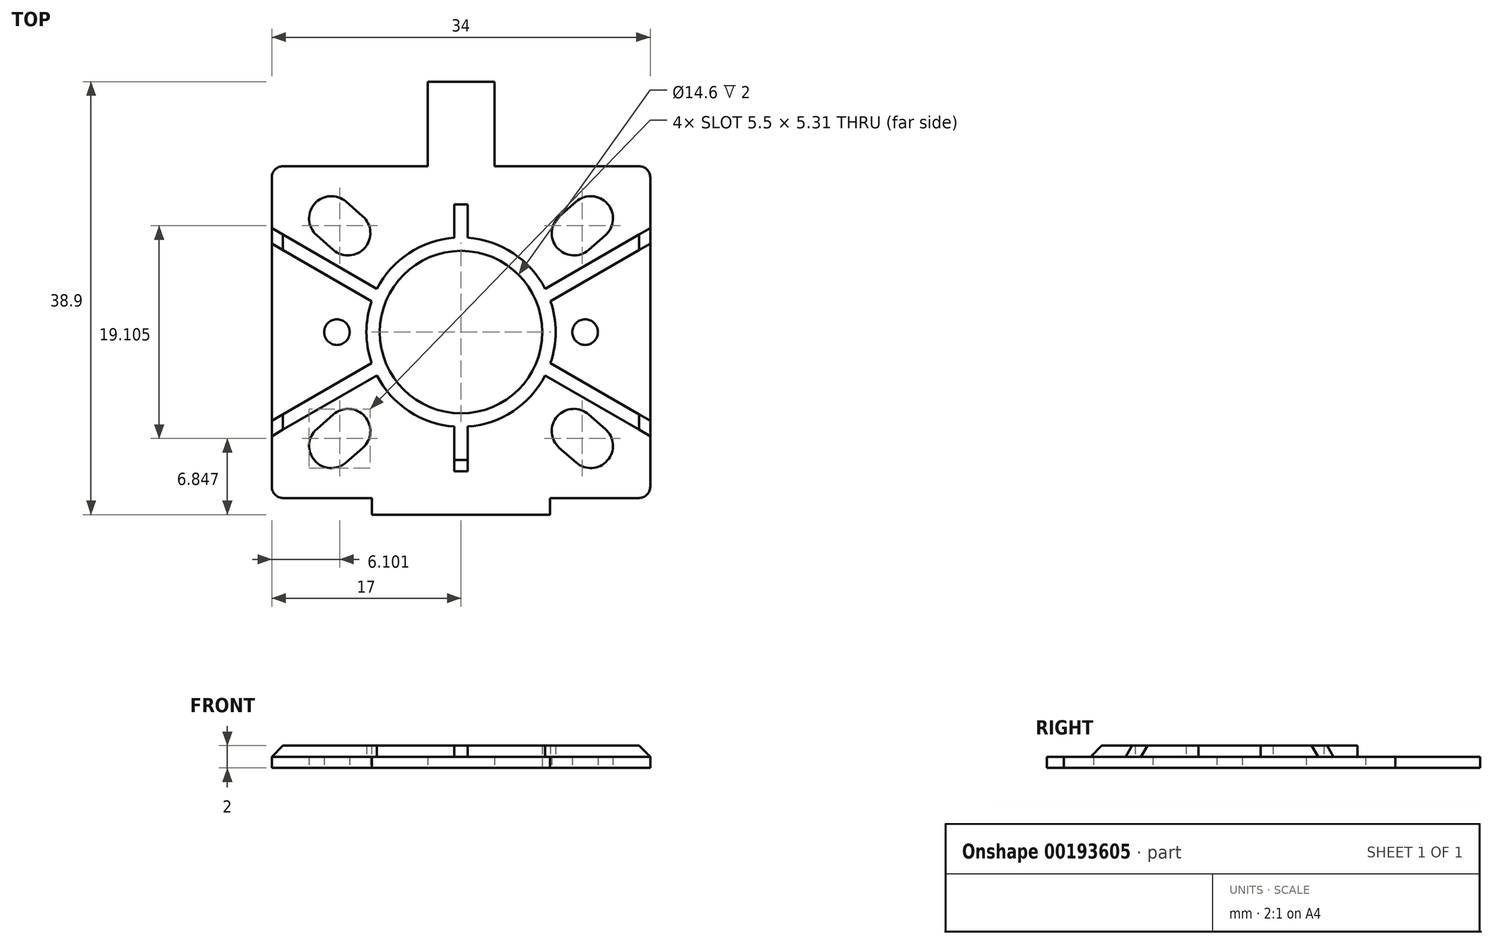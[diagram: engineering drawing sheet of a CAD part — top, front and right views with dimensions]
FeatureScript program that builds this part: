
annotation { "Feature Type Name" : "Feature", "Feature Type Description" : "" }
export const myFeature = defineFeature(function(context is Context, id is Id, definition is map)
    precondition{}
    {
        {
            var Q0;
            Q0=qCreatedBy(makeId("Top.planeOp"),FACE);
            var sketch = newSketch(context, id + "F0", { "sketchPlane" : qUnion([Q0])});
            skLineSegment(sketch, "E0.bottom", {"start": v(16, -14.9) * mm, "end": v(-16, -14.9) * mm});
            skLineSegment(sketch, "E0.top", {"start": v(16, 14.9) * mm, "end": v(-16, 14.9) * mm});
            skLineSegment(sketch, "E0.left", {"start": v(17, -13.9) * mm, "end": v(17, 13.9) * mm});
            skLineSegment(sketch, "E0.right", {"start": v(-17, -13.9) * mm, "end": v(-17, 13.9) * mm});
            skPoint(sketch, "E0.middle", {"position": v(0, 0) * mm});
            skCircle(sketch, "E1", {"center": v(0, 0) * mm, "radius": 7.3 * mm});
            skLineSegment(sketch, "E2", {"start": v(-11.15, 0) * mm, "end": v(11.15, 0) * mm, "construction": true});
            skCircle(sketch, "E3", {"center": v(-11.15, 0) * mm, "radius": 1.15 * mm});
            skCircle(sketch, "E4", {"center": v(11.15, 0) * mm, "radius": 1.15 * mm});
            skLineSegment(sketch, "E5.bottom", {"start": v(3, 14.9) * mm, "end": v(-3, 14.9) * mm});
            skLineSegment(sketch, "E5.top", {"start": v(3, 22.5) * mm, "end": v(-3, 22.5) * mm});
            skLineSegment(sketch, "E5.left", {"start": v(3, 14.9) * mm, "end": v(3, 22.5) * mm});
            skLineSegment(sketch, "E5.right", {"start": v(-3, 14.9) * mm, "end": v(-3, 22.5) * mm});
            skPoint(sketch, "E5.middle", {"position": v(0, 18.7) * mm});
            skLineSegment(sketch, "E6.bottom", {"start": v(8, -16.4) * mm, "end": v(-8, -16.4) * mm});
            skLineSegment(sketch, "E6.top", {"start": v(8, -14.9) * mm, "end": v(-8, -14.9) * mm});
            skLineSegment(sketch, "E6.left", {"start": v(8, -16.4) * mm, "end": v(8, -14.9) * mm});
            skLineSegment(sketch, "E6.right", {"start": v(-8, -16.4) * mm, "end": v(-8, -14.9) * mm});
            skPoint(sketch, "E6.middle", {"position": v(0, -15.65) * mm});
            skPoint(sketch, "E6.middle.positionSnap0", {"position": v(0, -14.9) * mm});
            skPoint(sketch, "E6.centerSnap0", {"position": v(0, -14.9) * mm});
            skLineSegment(sketch, "E7", {"start": v(-17, 14.9) * mm, "end": v(17, -14.9) * mm, "construction": true});
            skLineSegment(sketch, "E8", {"start": v(-17, -14.9) * mm, "end": v(17, 14.9) * mm, "construction": true});
            skLineSegment(sketch, "E9", {"start": v(0, -14.9) * mm, "end": v(0, 14.9) * mm, "construction": true});
            skPoint(sketch, "E10.visualSharp", {"position": v(-17, 14.9) * mm});
            skArc(sketch, "E10.filletArc", {"start": v(-16, 14.9) * mm, "mid": v(-16.7, 14.6) * mm, "end": v(-17, 13.9) * mm});
            skPoint(sketch, "E11.visualSharp", {"position": v(17, 14.9) * mm});
            skArc(sketch, "E11.filletArc", {"start": v(17, 13.9) * mm, "mid": v(16.7, 14.6) * mm, "end": v(16, 14.9) * mm});
            skPoint(sketch, "E12.visualSharp", {"position": v(17, -14.9) * mm});
            skArc(sketch, "E12.filletArc", {"start": v(16, -14.9) * mm, "mid": v(16.7, -14.6) * mm, "end": v(17, -13.9) * mm});
            skPoint(sketch, "E13.visualSharp", {"position": v(-17, -14.9) * mm});
            skArc(sketch, "E13.filletArc", {"start": v(-17, -13.9) * mm, "mid": v(-16.7, -14.6) * mm, "end": v(-16, -14.9) * mm});
            skLineSegment(sketch, "E14", {"start": v(-11.65, 10.21) * mm, "end": v(-10.15, 8.9) * mm, "construction": true});
            skArc(sketch, "E15.0.startCap", {"start": v(-12.97, 8.7) * mm, "mid": v(-13.15, 11.53) * mm, "end": v(-10.33, 11.72) * mm});
            skArc(sketch, "E15.0.endCap", {"start": v(-8.83, 10.4) * mm, "mid": v(-8.64, 7.58) * mm, "end": v(-11.47, 7.39) * mm});
            skLineSegment(sketch, "E15.0.left", {"start": v(-10.33, 11.72) * mm, "end": v(-8.83, 10.4) * mm});
            skLineSegment(sketch, "E15.0.right", {"start": v(-12.97, 8.7) * mm, "end": v(-11.47, 7.39) * mm});
            skLineSegment(sketch, "E16.MirrorCS", {"start": v(11.65, 10.21) * mm, "end": v(10.15, 8.9) * mm, "construction": true});
            skLineSegment(sketch, "E17.MirrorCS", {"start": v(12.97, 8.7) * mm, "end": v(11.47, 7.39) * mm});
            skArc(sketch, "E18.MirrorCS", {"start": v(8.83, 10.4) * mm, "mid": v(8.64, 7.58) * mm, "end": v(11.47, 7.39) * mm});
            skLineSegment(sketch, "E19.MirrorCS", {"start": v(10.33, 11.72) * mm, "end": v(8.83, 10.4) * mm});
            skArc(sketch, "E20.MirrorCS", {"start": v(12.97, 8.7) * mm, "mid": v(13.15, 11.53) * mm, "end": v(10.33, 11.72) * mm});
            skLineSegment(sketch, "E21.MirrorCS", {"start": v(10.33, -11.72) * mm, "end": v(8.83, -10.4) * mm});
            skLineSegment(sketch, "E22.MirrorCS", {"start": v(-10.33, -11.72) * mm, "end": v(-8.83, -10.4) * mm});
            skLineSegment(sketch, "E23.MirrorCS", {"start": v(-11.65, -10.21) * mm, "end": v(-10.15, -8.9) * mm, "construction": true});
            skLineSegment(sketch, "E24.MirrorCS", {"start": v(11.65, -10.21) * mm, "end": v(10.15, -8.9) * mm, "construction": true});
            skLineSegment(sketch, "E25.MirrorCS", {"start": v(-12.97, -8.7) * mm, "end": v(-11.47, -7.39) * mm});
            skLineSegment(sketch, "E26.MirrorCS", {"start": v(12.97, -8.7) * mm, "end": v(11.47, -7.39) * mm});
            skArc(sketch, "E27.MirrorCS", {"start": v(-8.83, -10.4) * mm, "mid": v(-8.64, -7.58) * mm, "end": v(-11.47, -7.39) * mm});
            skArc(sketch, "E28.MirrorCS", {"start": v(12.97, -8.7) * mm, "mid": v(13.15, -11.53) * mm, "end": v(10.33, -11.72) * mm});
            skArc(sketch, "E29.MirrorCS", {"start": v(-12.97, -8.7) * mm, "mid": v(-13.15, -11.53) * mm, "end": v(-10.33, -11.72) * mm});
            skArc(sketch, "E30.MirrorCS", {"start": v(8.83, -10.4) * mm, "mid": v(8.64, -7.58) * mm, "end": v(11.47, -7.39) * mm});
            skSolve(sketch);
        }
        {
            var Q0;
            Q0 = qSketchRegion(id + "F0", true);
            extrude(context, id + "F1", {"entities" : qUnion([Q0]), "depth" : 1 * mm});
        }
        {
            var Q0;
            Q0=makeQuery(id+"F1.opExtrude","CAP_FACE",FACE,{"disambiguationData":[OSD([sQuery(id+"F0.wireOp",EDGE,"E0.bottom"),sQuery(id+"F0.wireOp",EDGE,"E0.top"),sQuery(id+"F0.wireOp",EDGE,"E0.left"),sQuery(id+"F0.wireOp",EDGE,"E0.right"),sQuery(id+"F0.wireOp",EDGE,"E1"),sQuery(id+"F0.wireOp",EDGE,"E3"),sQuery(id+"F0.wireOp",EDGE,"E4"),sQuery(id+"F0.wireOp",EDGE,"E5.top"),sQuery(id+"F0.wireOp",EDGE,"E5.left"),sQuery(id+"F0.wireOp",EDGE,"E5.right"),sQuery(id+"F0.wireOp",EDGE,"E6.bottom"),sQuery(id+"F0.wireOp",EDGE,"E6.left"),sQuery(id+"F0.wireOp",EDGE,"E6.right"),sQuery(id+"F0.wireOp",EDGE,"Cg5mHujw-Crgq-w9C2-tdzf-h039JNJG8W8y"),sQuery(id+"F0.wireOp",EDGE,"Ps9XZvL5-BTdY-0Dsp-DGuL-4wo60B738f9t"),sQuery(id+"F0.wireOp",EDGE,"NziZYGv3-ZalC-V9XH-VD5N-91aEUs1mGeD4"),sQuery(id+"F0.wireOp",EDGE,"wrparZR5-Ca0K-EmIK-8Wlq-3zDmcIoanExd"),sQuery(id+"F0.wireOp",EDGE,"30673667-c7c9-486b-8852-d69ce27fa3a1.filletArc"),sQuery(id+"F0.wireOp",EDGE,"ba702d56-8ab8-4f31-9c18-c75d7e6bf162.filletArc"),sQuery(id+"F0.wireOp",EDGE,"61057ac9-38be-461f-bca9-094edfcdb327.filletArc"),sQuery(id+"F0.wireOp",EDGE,"a9f16732-ca3d-4a78-8be7-feecf1bcdde3.filletArc"),sQuery(id+"F0.wireOp",EDGE,"0958a51f-cc26-4892-b37d-54eeb7879d5b0.MirrorCS"),sQuery(id+"F0.wireOp",EDGE,"0958a51f-cc26-4892-b37d-54eeb7879d5b1.MirrorCS"),sQuery(id+"F0.wireOp",EDGE,"0958a51f-cc26-4892-b37d-54eeb7879d5b2.MirrorCS"),sQuery(id+"F0.wireOp",EDGE,"0958a51f-cc26-4892-b37d-54eeb7879d5b3.MirrorCS"),sQuery(id+"F0.wireOp",EDGE,"0958a51f-cc26-4892-b37d-54eeb7879d5b4.MirrorCS"),sQuery(id+"F0.wireOp",EDGE,"0958a51f-cc26-4892-b37d-54eeb7879d5b6.MirrorCS"),sQuery(id+"F0.wireOp",EDGE,"0958a51f-cc26-4892-b37d-54eeb7879d5b8.MirrorCS"),sQuery(id+"F0.wireOp",EDGE,"0958a51f-cc26-4892-b37d-54eeb7879d5b11.MirrorCS"),sQuery(id+"F0.wireOp",EDGE,"47bd3fab-0a37-40e4-8793-955853e768a70.MirrorCS"),sQuery(id+"F0.wireOp",EDGE,"47bd3fab-0a37-40e4-8793-955853e768a71.MirrorCS"),sQuery(id+"F0.wireOp",EDGE,"47bd3fab-0a37-40e4-8793-955853e768a72.MirrorCS"),sQuery(id+"F0.wireOp",EDGE,"47bd3fab-0a37-40e4-8793-955853e768a73.MirrorCS"),sQuery(id+"F0.wireOp",EDGE,"47bd3fab-0a37-40e4-8793-955853e768a74.MirrorCS"),sQuery(id+"F0.wireOp",EDGE,"47bd3fab-0a37-40e4-8793-955853e768a75.MirrorCS"),sQuery(id+"F0.wireOp",EDGE,"47bd3fab-0a37-40e4-8793-955853e768a76.MirrorCS"),sQuery(id+"F0.wireOp",EDGE,"47bd3fab-0a37-40e4-8793-955853e768a77.MirrorCS"),sQuery(id+"F0.wireOp",EDGE,"47bd3fab-0a37-40e4-8793-955853e768a78.MirrorCS"),sQuery(id+"F0.wireOp",EDGE,"47bd3fab-0a37-40e4-8793-955853e768a79.MirrorCS"),sQuery(id+"F0.wireOp",EDGE,"47bd3fab-0a37-40e4-8793-955853e768a710.MirrorCS"),sQuery(id+"F0.wireOp",EDGE,"47bd3fab-0a37-40e4-8793-955853e768a711.MirrorCS"),sQuery(id+"F0.wireOp",EDGE,"47bd3fab-0a37-40e4-8793-955853e768a712.MirrorCS"),sQuery(id+"F0.wireOp",EDGE,"47bd3fab-0a37-40e4-8793-955853e768a718.MirrorCS"),sQuery(id+"F0.wireOp",EDGE,"47bd3fab-0a37-40e4-8793-955853e768a722.MirrorCS"),sQuery(id+"F0.wireOp",EDGE,"47bd3fab-0a37-40e4-8793-955853e768a723.MirrorCS"),sQuery(id+"F0.wireOp",EDGE,"E10.filletArc"),sQuery(id+"F0.wireOp",EDGE,"E11.filletArc"),sQuery(id+"F0.wireOp",EDGE,"E12.filletArc"),sQuery(id+"F0.wireOp",EDGE,"E13.filletArc")])],"isStart":false});
            var sketch = newSketch(context, id + "F2", { "sketchPlane" : qUnion([Q0])});
            skCircle(sketch, "E31.0", {"center": v(0, 0) * mm, "radius": 7.3 * mm});
            skCircle(sketch, "E32.0", {"center": v(0, 0) * mm, "radius": 8.5 * mm});
            skLineSegment(sketch, "E33", {"start": v(0, 14.9) * mm, "end": v(0, -14.9) * mm, "construction": true});
            skLineSegment(sketch, "E34", {"start": v(-17, 0) * mm, "end": v(17, 0) * mm, "construction": true});
            skLineSegment(sketch, "E35", {"start": v(-17, 9.34) * mm, "end": v(-7.56, 3.9) * mm});
            skLineSegment(sketch, "E36", {"start": v(-17, 7.96) * mm, "end": v(-8.03, 2.78) * mm});
            skLineSegment(sketch, "E37.MirrorCS", {"start": v(-17, -7.96) * mm, "end": v(-8.03, -2.78) * mm});
            skLineSegment(sketch, "E38.MirrorCS", {"start": v(-17, -9.34) * mm, "end": v(-7.56, -3.9) * mm});
            skLineSegment(sketch, "E39.MirrorCS", {"start": v(17, 9.34) * mm, "end": v(7.56, 3.9) * mm});
            skLineSegment(sketch, "E40.MirrorCS", {"start": v(17, 7.96) * mm, "end": v(8.03, 2.78) * mm});
            skLineSegment(sketch, "E41.MirrorCS", {"start": v(17, -7.96) * mm, "end": v(8.03, -2.78) * mm});
            skLineSegment(sketch, "E42.MirrorCS", {"start": v(17, -9.34) * mm, "end": v(7.56, -3.9) * mm});
            skLineSegment(sketch, "E43.bottom", {"start": v(0.6, 7.3) * mm, "end": v(-0.6, 7.3) * mm});
            skLineSegment(sketch, "E43.top", {"start": v(0.6, 11.48) * mm, "end": v(-0.6, 11.48) * mm});
            skLineSegment(sketch, "E43.left", {"start": v(0.6, 7.3) * mm, "end": v(0.6, 11.48) * mm});
            skLineSegment(sketch, "E43.right", {"start": v(-0.6, 7.3) * mm, "end": v(-0.6, 11.48) * mm});
            skPoint(sketch, "E43.middle", {"position": v(0, 9.4) * mm});
            skLineSegment(sketch, "E44.MirrorCS", {"start": v(0.6, -11.48) * mm, "end": v(-0.6, -11.48) * mm});
            skLineSegment(sketch, "E45.MirrorCS", {"start": v(0.6, -7.3) * mm, "end": v(-0.6, -7.3) * mm});
            skPoint(sketch, "E46.MirrorP", {"position": v(0, -9.4) * mm});
            skLineSegment(sketch, "E47.MirrorCS", {"start": v(-0.6, -7.3) * mm, "end": v(-0.6, -11.48) * mm});
            skLineSegment(sketch, "E48.MirrorCS", {"start": v(0.6, -7.3) * mm, "end": v(0.6, -11.48) * mm});
            skSolve(sketch);
        }
        {
            var Q0;
            Q0 = qSketchRegion(id + "F2", true);
            var Q1;
            {var subQ7=sQuery(id+"F2.wireOp",EDGE,"E36");Q1=makeQuery(id+"F2.imprint","IMPRINT",FACE,{"disambiguationData":[TD([[makeQuery(id+"F2.imprint","IMPRINT",EDGE,{"derivedFrom":subQ7}),1.0]])]});}
            var Q2;
            {var subQ3=sQuery(id+"F2.wireOp",EDGE,"E37.MirrorCS");Q2=makeQuery(id+"F2.imprint","IMPRINT",FACE,{"disambiguationData":[TD([[makeQuery(id+"F2.imprint","IMPRINT",EDGE,{"derivedFrom":subQ3}),-1.0]])]});}
            var Q3;
            {var subQ3=sQuery(id+"F2.wireOp",EDGE,"E41.MirrorCS");Q3=makeQuery(id+"F2.imprint","IMPRINT",FACE,{"disambiguationData":[TD([[makeQuery(id+"F2.imprint","IMPRINT",EDGE,{"derivedFrom":subQ3}),1.0]])]});}
            var Q4;
            {var subQ7=sQuery(id+"F2.wireOp",EDGE,"E40.MirrorCS");Q4=makeQuery(id+"F2.imprint","IMPRINT",FACE,{"disambiguationData":[TD([[makeQuery(id+"F2.imprint","IMPRINT",EDGE,{"derivedFrom":subQ7}),-1.0]])]});}
            extrude(context, id + "F3", {"entities" : qUnion([Q0, Q1, Q2, Q3, Q4]), "operationType" : NewBodyOperationType.ADD, "depth" : 1 * mm});
        }
        {
            var Q0;
            Q0=makeQuery(id+"F3.opExtrude","CAP_EDGE",EDGE,{"disambiguationData":[OSD([sQuery(id+"F2.wireOp",EDGE,"E43.top")])],"isStart":true});
            var Q1;
            Q1=makeQuery(id+"F3.opExtrude","CAP_EDGE",EDGE,{"disambiguationData":[OSD([sQuery(id+"F2.wireOp",EDGE,"E44.MirrorCS")])],"isStart":true});
            var Q2;
            {var subQ0=sQuery(id+"F0.wireOp",EDGE,"E0.right");var subQ1=makeQuery(id+"F1.opExtrude","CAP_EDGE",EDGE,{"disambiguationData":[OSD([subQ0])],"isStart":false});Q2=makeQuery(id+"F3.opExtrude","CAP_EDGE",EDGE,{"disambiguationData":[OSD([subQ0]),TDD([makeQuery(id+"F2.imprint","IMPRINT",EDGE,{"disambiguationData":[TD([[makeQuery(id+"F2.imprint","INTERSECT",VERTEX,{"derivedFrom":[subQ1,sQuery(id+"F2.wireOp",EDGE,"E37.MirrorCS")]}),1.0]])],"derivedFrom":subQ1})])],"isStart":false});}
            var Q3;
            {var subQ0=sQuery(id+"F0.wireOp",EDGE,"E0.left");var subQ1=makeQuery(id+"F1.opExtrude","CAP_EDGE",EDGE,{"disambiguationData":[OSD([subQ0])],"isStart":false});Q3=makeQuery(id+"F3.opExtrude","CAP_EDGE",EDGE,{"disambiguationData":[OSD([subQ0]),TDD([makeQuery(id+"F2.imprint","IMPRINT",EDGE,{"disambiguationData":[TD([[makeQuery(id+"F2.imprint","INTERSECT",VERTEX,{"derivedFrom":[subQ1,sQuery(id+"F2.wireOp",EDGE,"E41.MirrorCS")]}),1.0]])],"derivedFrom":subQ1})])],"isStart":false});}
            var Q4;
            {var subQ0=sQuery(id+"F0.wireOp",EDGE,"E0.right");var subQ1=makeQuery(id+"F1.opExtrude","CAP_EDGE",EDGE,{"disambiguationData":[OSD([subQ0])],"isStart":false});Q4=makeQuery(id+"F3.opExtrude","CAP_EDGE",EDGE,{"disambiguationData":[OSD([subQ0]),TDD([makeQuery(id+"F2.imprint","IMPRINT",EDGE,{"disambiguationData":[TD([[makeQuery(id+"F2.imprint","INTERSECT",VERTEX,{"derivedFrom":[subQ1,sQuery(id+"F2.wireOp",EDGE,"E35")]}),1.0]])],"derivedFrom":subQ1})])],"isStart":false});}
            var Q5;
            {var subQ0=sQuery(id+"F0.wireOp",EDGE,"E0.left");var subQ1=makeQuery(id+"F1.opExtrude","CAP_EDGE",EDGE,{"disambiguationData":[OSD([subQ0])],"isStart":false});Q5=makeQuery(id+"F3.opExtrude","CAP_EDGE",EDGE,{"disambiguationData":[OSD([subQ0]),TDD([makeQuery(id+"F2.imprint","IMPRINT",EDGE,{"disambiguationData":[TD([[makeQuery(id+"F2.imprint","INTERSECT",VERTEX,{"derivedFrom":[subQ1,sQuery(id+"F2.wireOp",EDGE,"E39.MirrorCS")]}),1.0]])],"derivedFrom":subQ1})])],"isStart":false});}
            chamfer(context, id + "F4", {"entities" : qUnion([Q0, Q1, Q2, Q3, Q4, Q5]), "width" : 1 * mm, "tangentPropagation" : true});
        }
    });
